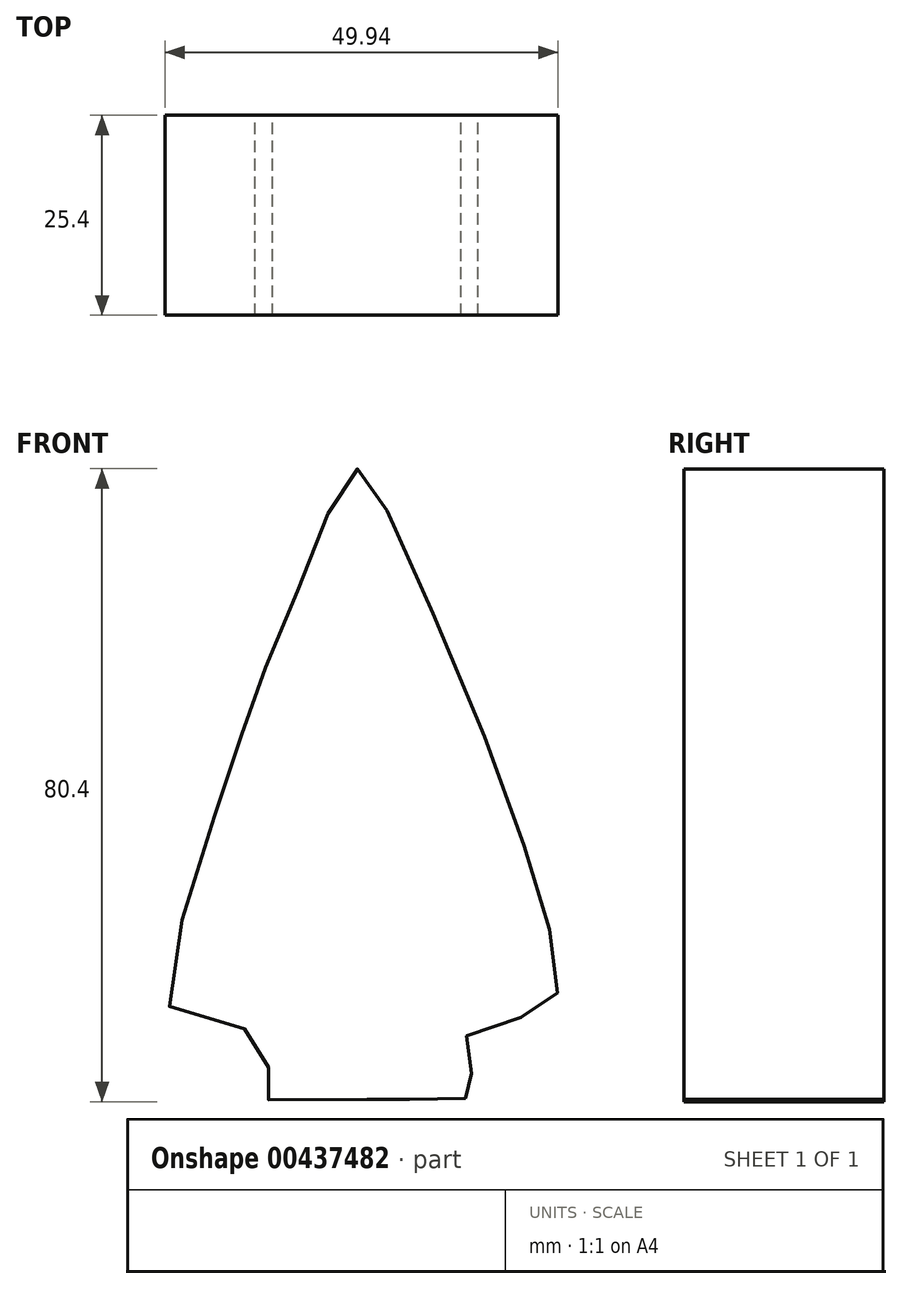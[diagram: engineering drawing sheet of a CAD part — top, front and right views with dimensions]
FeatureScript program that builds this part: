
annotation { "Feature Type Name" : "Feature", "Feature Type Description" : "" }
export const myFeature = defineFeature(function(context is Context, id is Id, definition is map)
    precondition{}
    {
        {
            var Q0;
            Q0=qCreatedBy(makeId("Front.planeOp"),FACE);
            var sketch = newSketch(context, id + "F0", { "sketchPlane" : qUnion([Q0])});
            skPoint(sketch, "E0.16.internal.snap0", {"position": v(-1.21, 56.49) * mm});
            skFitSpline(sketch, "E0", {"points": [v(0, -10.63) * mm, v(2.93, -10.63) * mm, v(6.47, -10.56) * mm, v(11.93, -10.48) * mm, v(13.81, -10.06) * mm, v(13.95, -8.5) * mm, v(12.26, -5.75) * mm, v(12.18, -3.35) * mm, v(14.56, -1.2) * mm, v(21.3, 0.15) * mm, v(23.82, 1.74) * mm, v(24.1, 6.65) * mm, v(21.9, 15.5) * mm, v(15.86, 33.18) * mm, v(5.07, 58.64) * mm, v(0.1, 68.72) * mm, v(-1.21, 69.49) * mm, v(-3.43, 67.2) * mm, v(-6.85, 58.67) * mm, v(-11.72, 47.38) * mm, v(-14.75, 38.86) * mm, v(-17.98, 29.85) * mm, v(-23.45, 12.38) * mm, v(-24.68, 0.66) * mm, v(-14.34, -1.98) * mm, v(-12.01, -5.12) * mm, v(-13.94, -8.81) * mm, v(-13.82, -10.3) * mm, v(0, -10.63) * mm]});
            skSolve(sketch);
        }
        {
            var Q0;
            Q0 = qSketchRegion(id + "F0", true);
            extrude(context, id + "F1", {"entities" : qUnion([Q0]), "endBound" : BoundingType.SYMMETRIC, "depth" : 25.4 * mm});
        }
    });
